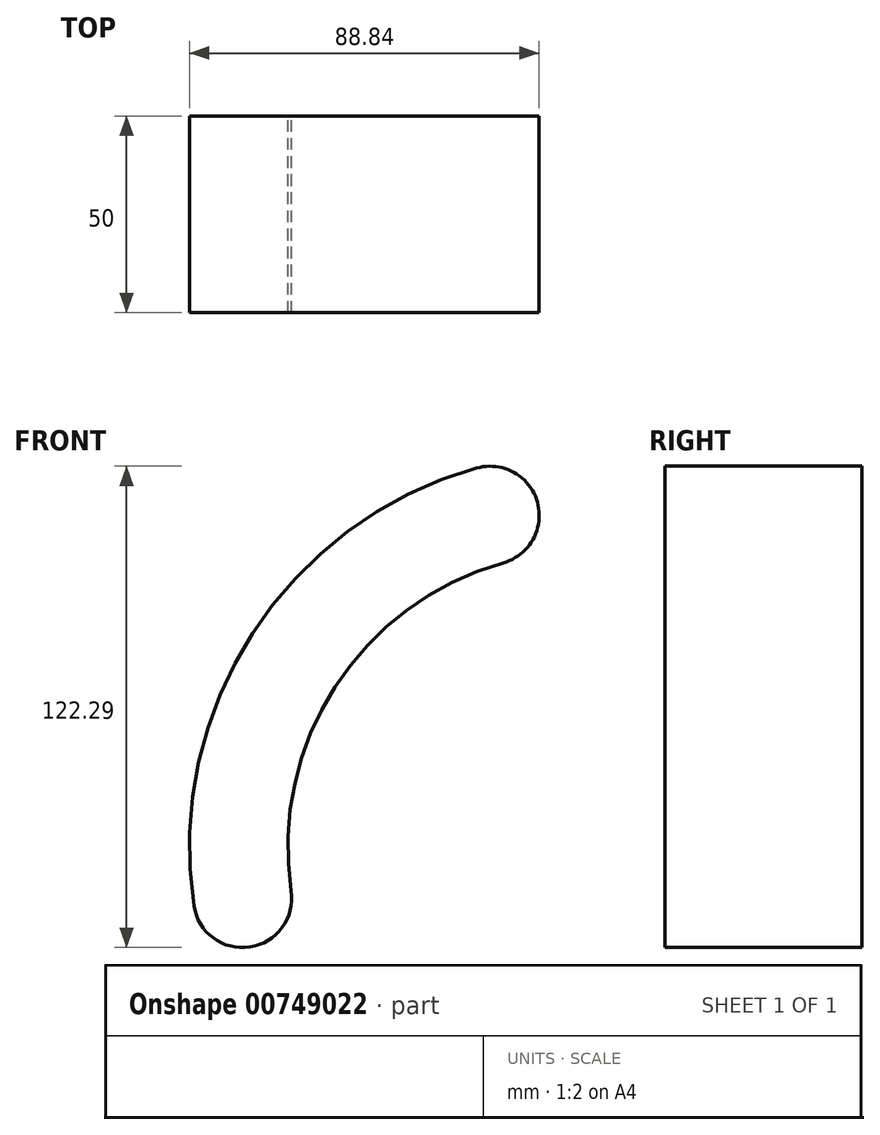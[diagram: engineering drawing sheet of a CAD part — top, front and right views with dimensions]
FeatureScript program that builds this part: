
annotation { "Feature Type Name" : "Feature", "Feature Type Description" : "" }
export const myFeature = defineFeature(function(context is Context, id is Id, definition is map)
    precondition{}
    {
        {
            var Q0;
            Q0=qCreatedBy(makeId("Front.planeOp"),FACE);
            var sketch = newSketch(context, id + "F0", { "sketchPlane" : qUnion([Q0])});
            skCircle(sketch, "E0", {"center": v(0, 0) * mm, "radius": 100 * mm});
            skCircle(sketch, "E1", {"center": v(0, 0) * mm, "radius": 75 * mm});
            skCircle(sketch, "E2", {"center": v(-23.66, 84.24) * mm, "radius": 12.5 * mm});
            skCircle(sketch, "E3", {"center": v(-23.66, 84.24) * mm, "radius": 7.5 * mm});
            skCircle(sketch, "E4", {"center": v(-86.52, -13.05) * mm, "radius": 12.5 * mm});
            skCircle(sketch, "E5", {"center": v(-86.52, -13.05) * mm, "radius": 7.5 * mm});
            skSolve(sketch);
        }
        {
            var Q0;
            {var subQ0=sQuery(id+"F0.wireOp",EDGE,"E2");var subQ1=sQuery(id+"F0.wireOp",EDGE,"E0");var subQ2=makeQuery(id+"F0.imprint","INTERSECT",VERTEX,{"derivedFrom":[subQ1,subQ0]});Q0=makeQuery(id+"F0.imprint","IMPRINT",FACE,{"disambiguationData":[TD([[makeQuery(id+"F0.imprint","IMPRINT",EDGE,{"disambiguationData":[TD([[subQ2,-1.0]])],"derivedFrom":subQ1}),1.0]])]});}
            var sketch = newSketch(context, id + "F1", { "sketchPlane" : qUnion([Q0])});
            skSolve(sketch);
        }
        {
            var Q0;
            Q0 = qSketchRegion(id + "F1", true);
            var Q1;
            {var subQ0=sQuery(id+"F0.wireOp",EDGE,"E2");var subQ1=sQuery(id+"F0.wireOp",EDGE,"E0");var subQ2=makeQuery(id+"F0.imprint","INTERSECT",VERTEX,{"derivedFrom":[subQ1,subQ0]});Q1=makeQuery(id+"F0.imprint","IMPRINT",FACE,{"disambiguationData":[TD([[makeQuery(id+"F0.imprint","IMPRINT",EDGE,{"disambiguationData":[TD([[subQ2,-1.0]])],"derivedFrom":subQ1}),1.0]])]});}
            var Q2;
            Q2=makeQuery(id+"F0.imprint","IMPRINT",FACE,{"disambiguationData":[TD([[makeQuery(id+"F0.imprint","IMPRINT",EDGE,{"derivedFrom":sQuery(id+"F0.wireOp",EDGE,"E3")}),1.0]])]});
            var Q3;
            Q3=makeQuery(id+"F0.imprint","IMPRINT",FACE,{"disambiguationData":[TD([[makeQuery(id+"F0.imprint","IMPRINT",EDGE,{"derivedFrom":sQuery(id+"F0.wireOp",EDGE,"E3")}),-1.0]])]});
            var Q4;
            Q4=makeQuery(id+"F0.imprint","IMPRINT",FACE,{"disambiguationData":[TD([[makeQuery(id+"F0.imprint","IMPRINT",EDGE,{"derivedFrom":sQuery(id+"F0.wireOp",EDGE,"E5")}),-1.0]])]});
            var Q5;
            Q5=makeQuery(id+"F0.imprint","IMPRINT",FACE,{"disambiguationData":[TD([[makeQuery(id+"F0.imprint","IMPRINT",EDGE,{"derivedFrom":sQuery(id+"F0.wireOp",EDGE,"E5")}),1.0]])]});
            extrude(context, id + "F2", {"entities" : qUnion([Q0, Q1, Q2, Q3, Q4, Q5]), "depth" : 50 * mm, "offsetDistance" : 25 * mm});
        }
    });
